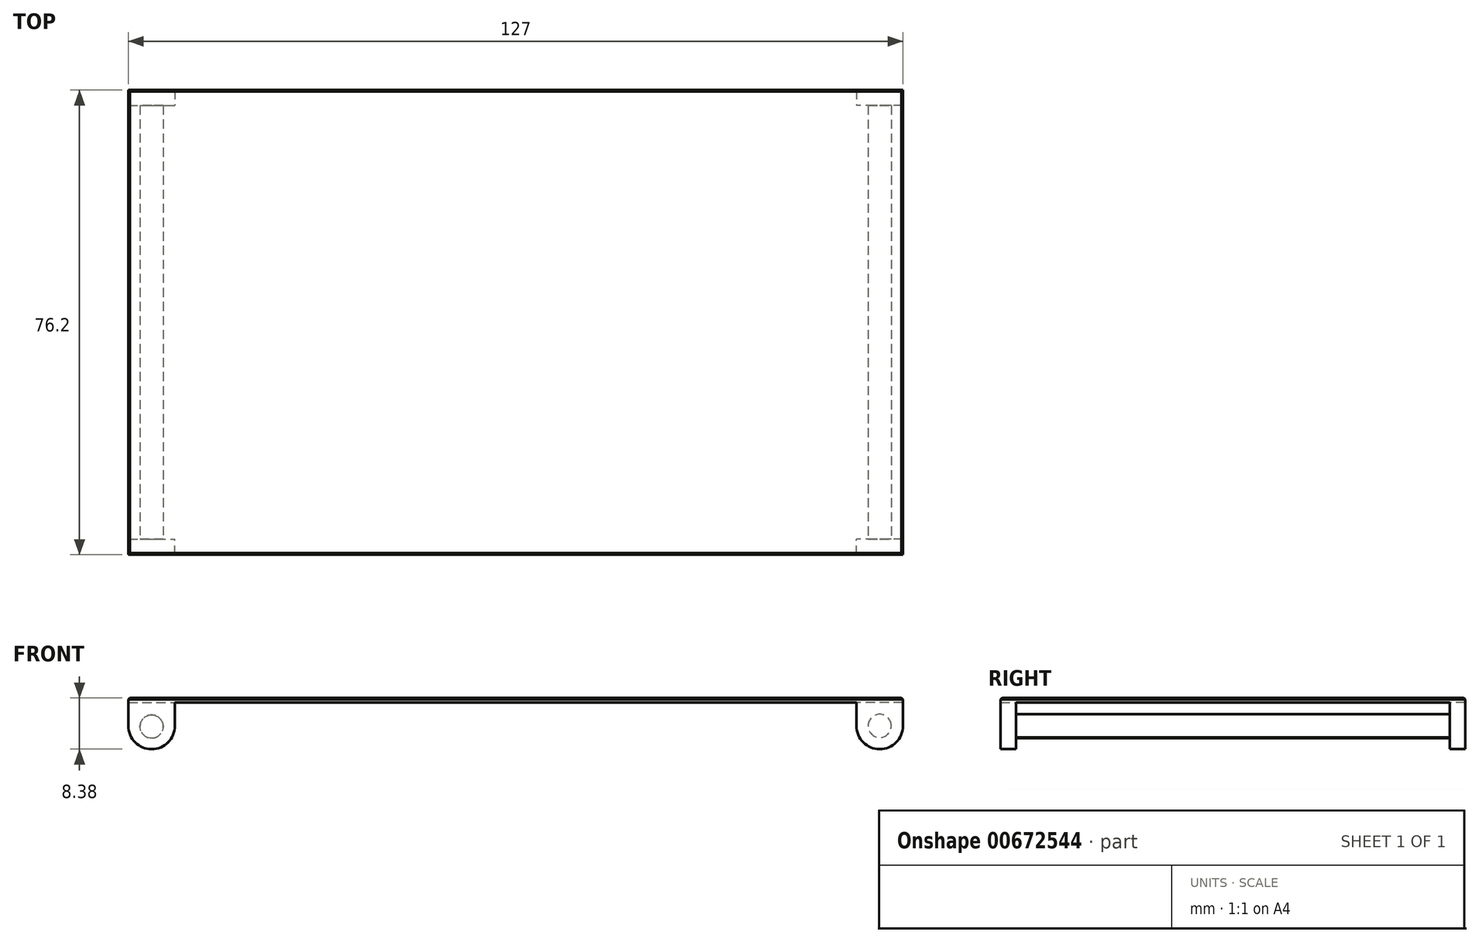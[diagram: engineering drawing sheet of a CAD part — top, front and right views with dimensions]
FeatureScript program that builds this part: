
annotation { "Feature Type Name" : "Feature", "Feature Type Description" : "" }
export const myFeature = defineFeature(function(context is Context, id is Id, definition is map)
    precondition{}
    {
        {
            var Q0;
            Q0=qCreatedBy(makeId("Top.planeOp"),FACE);
            var sketch = newSketch(context, id + "F0", { "sketchPlane" : qUnion([Q0])});
            skLineSegment(sketch, "E0.bottom", {"start": v(-63.64, 83.81) * mm, "end": v(63.36, 83.81) * mm});
            skLineSegment(sketch, "E0.top", {"start": v(-63.64, 7.61) * mm, "end": v(63.36, 7.61) * mm});
            skLineSegment(sketch, "E0.left", {"start": v(-63.64, 83.81) * mm, "end": v(-63.64, 7.61) * mm});
            skLineSegment(sketch, "E0.right", {"start": v(63.36, 83.81) * mm, "end": v(63.36, 7.61) * mm});
            skSolve(sketch);
        }
        {
            var Q0;
            Q0=makeQuery(id+"F0.imprint","IMPRINT",FACE,{"disambiguationData":[TD([[makeQuery(id+"F0.imprint","IMPRINT",EDGE,{"derivedFrom":sQuery(id+"F0.wireOp",EDGE,"E0.bottom")}),-1.0]])]});
            extrude(context, id + "F1", {"entities" : qUnion([Q0]), "depth" : 0.76 * mm, "offsetDistance" : 25.4 * mm});
        }
        {
            var Q0;
            Q0=makeQuery(id+"F1.opExtrude","CAP_FACE",FACE,{"disambiguationData":[OSD([sQuery(id+"F0.wireOp",EDGE,"E0.bottom"),sQuery(id+"F0.wireOp",EDGE,"E0.top"),sQuery(id+"F0.wireOp",EDGE,"E0.left"),sQuery(id+"F0.wireOp",EDGE,"E0.right")])],"isStart":true});
            var sketch = newSketch(context, id + "F2", { "sketchPlane" : qUnion([Q0])});
            skLineSegment(sketch, "E1.bottom", {"start": v(-63.64, -7.61) * mm, "end": v(-56.02, -7.61) * mm});
            skLineSegment(sketch, "E1.top", {"start": v(-63.64, -10.15) * mm, "end": v(-56.02, -10.15) * mm});
            skLineSegment(sketch, "E1.left", {"start": v(-63.64, -7.61) * mm, "end": v(-63.64, -10.15) * mm});
            skLineSegment(sketch, "E1.right", {"start": v(-56.02, -7.61) * mm, "end": v(-56.02, -10.15) * mm});
            skLineSegment(sketch, "E2.bottom", {"start": v(63.36, -7.61) * mm, "end": v(55.74, -7.61) * mm});
            skLineSegment(sketch, "E2.top", {"start": v(63.36, -10.16) * mm, "end": v(55.74, -10.16) * mm});
            skLineSegment(sketch, "E2.left", {"start": v(63.36, -7.61) * mm, "end": v(63.36, -10.16) * mm});
            skLineSegment(sketch, "E2.right", {"start": v(55.74, -7.61) * mm, "end": v(55.74, -10.16) * mm});
            skLineSegment(sketch, "E3.bottom", {"start": v(63.36, -83.81) * mm, "end": v(55.74, -83.81) * mm});
            skLineSegment(sketch, "E3.top", {"start": v(63.36, -81.27) * mm, "end": v(55.74, -81.27) * mm});
            skLineSegment(sketch, "E3.left", {"start": v(63.36, -83.81) * mm, "end": v(63.36, -81.27) * mm});
            skLineSegment(sketch, "E3.right", {"start": v(55.74, -83.81) * mm, "end": v(55.74, -81.27) * mm});
            skLineSegment(sketch, "E4.bottom", {"start": v(-63.64, -83.81) * mm, "end": v(-56, -83.81) * mm});
            skLineSegment(sketch, "E4.top", {"start": v(-63.64, -81.28) * mm, "end": v(-56, -81.28) * mm});
            skLineSegment(sketch, "E4.left", {"start": v(-63.64, -83.81) * mm, "end": v(-63.64, -81.28) * mm});
            skLineSegment(sketch, "E4.right", {"start": v(-56, -83.81) * mm, "end": v(-56, -81.28) * mm});
            skSolve(sketch);
        }
        {
            var Q0;
            Q0=makeQuery(id+"F2.imprint","IMPRINT",FACE,{"disambiguationData":[TD([[makeQuery(id+"F2.imprint","IMPRINT",EDGE,{"derivedFrom":sQuery(id+"F2.wireOp",EDGE,"E1.bottom")}),-1.0]])]});
            var Q1;
            Q1=makeQuery(id+"F2.imprint","IMPRINT",FACE,{"disambiguationData":[TD([[makeQuery(id+"F2.imprint","IMPRINT",EDGE,{"derivedFrom":sQuery(id+"F2.wireOp",EDGE,"E4.bottom")}),1.0]])]});
            var Q2;
            Q2=makeQuery(id+"F2.imprint","IMPRINT",FACE,{"disambiguationData":[TD([[makeQuery(id+"F2.imprint","IMPRINT",EDGE,{"derivedFrom":sQuery(id+"F2.wireOp",EDGE,"E3.bottom")}),1.0]])]});
            var Q3;
            Q3=makeQuery(id+"F2.imprint","IMPRINT",FACE,{"disambiguationData":[TD([[makeQuery(id+"F2.imprint","IMPRINT",EDGE,{"derivedFrom":sQuery(id+"F2.wireOp",EDGE,"E2.bottom")}),-1.0]])]});
            extrude(context, id + "F3", {"entities" : qUnion([Q0, Q1, Q2, Q3]), "operationType" : NewBodyOperationType.ADD, "depth" : 7.62 * mm, "offsetDistance" : 25.4 * mm});
        }
        {
            var Q0;
            Q0=makeQuery(id+"F3.opExtrude","SWEPT_FACE",FACE,{"disambiguationData":[OSD([sQuery(id+"F2.wireOp",EDGE,"E1.top")])]});
            var sketch = newSketch(context, id + "F4", { "sketchPlane" : qUnion([Q0])});
            skCircle(sketch, "E5", {"center": v(59.82, -3.92) * mm, "radius": 1.9 * mm});
            skSolve(sketch);
        }
        {
            var Q0;
            Q0 = qSketchRegion(id + "F4", true);
            extrude(context, id + "F5", {"entities" : qUnion([Q0]), "operationType" : NewBodyOperationType.ADD, "depth" : 71.12 * mm, "offsetDistance" : 25.4 * mm});
        }
        {
            var Q0;
            Q0=makeQuery(id+"F3.opExtrude","SWEPT_FACE",FACE,{"disambiguationData":[OSD([sQuery(id+"F2.wireOp",EDGE,"E2.top")])]});
            var sketch = newSketch(context, id + "F6", { "sketchPlane" : qUnion([Q0])});
            skCircle(sketch, "E6", {"center": v(-59.55, -3.8) * mm, "radius": 1.9 * mm});
            skPoint(sketch, "E6.centerSnap0", {"position": v(-63.36, -3.81) * mm});
            skSolve(sketch);
        }
        {
            var Q0;
            Q0=makeQuery(id+"F6.imprint","IMPRINT",FACE,{"disambiguationData":[TD([[makeQuery(id+"F6.imprint","IMPRINT",EDGE,{"derivedFrom":sQuery(id+"F6.wireOp",EDGE,"E6")}),1.0]])]});
            extrude(context, id + "F7", {"entities" : qUnion([Q0]), "operationType" : NewBodyOperationType.ADD, "depth" : 71.12 * mm, "offsetDistance" : 25.4 * mm});
        }
        {
            var Q0;
            Q0=makeQuery(id+"F3.opExtrude","CAP_EDGE",EDGE,{"disambiguationData":[OSD([sQuery(id+"F2.wireOp",EDGE,"E3.right")])],"isStart":false});
            var Q1;
            Q1=makeQuery(id+"F3.opExtrude","CAP_EDGE",EDGE,{"disambiguationData":[OSD([sQuery(id+"F2.wireOp",EDGE,"E3.left")])],"isStart":false});
            var Q2;
            Q2=makeQuery(id+"F3.opExtrude","CAP_EDGE",EDGE,{"disambiguationData":[OSD([sQuery(id+"F2.wireOp",EDGE,"E2.left")])],"isStart":false});
            var Q3;
            Q3=makeQuery(id+"F3.opExtrude","CAP_EDGE",EDGE,{"disambiguationData":[OSD([sQuery(id+"F2.wireOp",EDGE,"E2.right")])],"isStart":false});
            var Q4;
            Q4=makeQuery(id+"F3.opExtrude","CAP_EDGE",EDGE,{"disambiguationData":[OSD([sQuery(id+"F2.wireOp",EDGE,"E1.right")])],"isStart":false});
            var Q5;
            Q5=makeQuery(id+"F3.opExtrude","CAP_EDGE",EDGE,{"disambiguationData":[OSD([sQuery(id+"F2.wireOp",EDGE,"E1.left")])],"isStart":false});
            var Q6;
            Q6=makeQuery(id+"F3.opExtrude","CAP_EDGE",EDGE,{"disambiguationData":[OSD([sQuery(id+"F2.wireOp",EDGE,"E4.right")])],"isStart":false});
            var Q7;
            Q7=makeQuery(id+"F3.opExtrude","CAP_EDGE",EDGE,{"disambiguationData":[OSD([sQuery(id+"F2.wireOp",EDGE,"E4.left")])],"isStart":false});
            fillet(context, id + "F8", {"entities" : qUnion([Q0, Q1, Q2, Q3, Q4, Q5, Q6, Q7]), "radius" : 3.8 * mm, "tangentPropagation" : true, "allowEdgeOverflow" : false});
        }
        {
            var Q0;
            Q0=makeQuery(id+"F1.opExtrude","CAP_EDGE",EDGE,{"disambiguationData":[OSD([sQuery(id+"F0.wireOp",EDGE,"E0.right")])],"isStart":false});
            var Q1;
            Q1=makeQuery(id+"F1.opExtrude","CAP_EDGE",EDGE,{"disambiguationData":[OSD([sQuery(id+"F0.wireOp",EDGE,"E0.bottom")])],"isStart":false});
            var Q2;
            Q2=makeQuery(id+"F1.opExtrude","CAP_EDGE",EDGE,{"disambiguationData":[OSD([sQuery(id+"F0.wireOp",EDGE,"E0.left")])],"isStart":false});
            var Q3;
            Q3=makeQuery(id+"F1.opExtrude","CAP_EDGE",EDGE,{"disambiguationData":[OSD([sQuery(id+"F0.wireOp",EDGE,"E0.top")])],"isStart":false});
            chamfer(context, id + "F9", {"entities" : qUnion([Q0, Q1, Q2, Q3]), "width" : 0.25 * mm, "tangentPropagation" : true});
        }
    });
